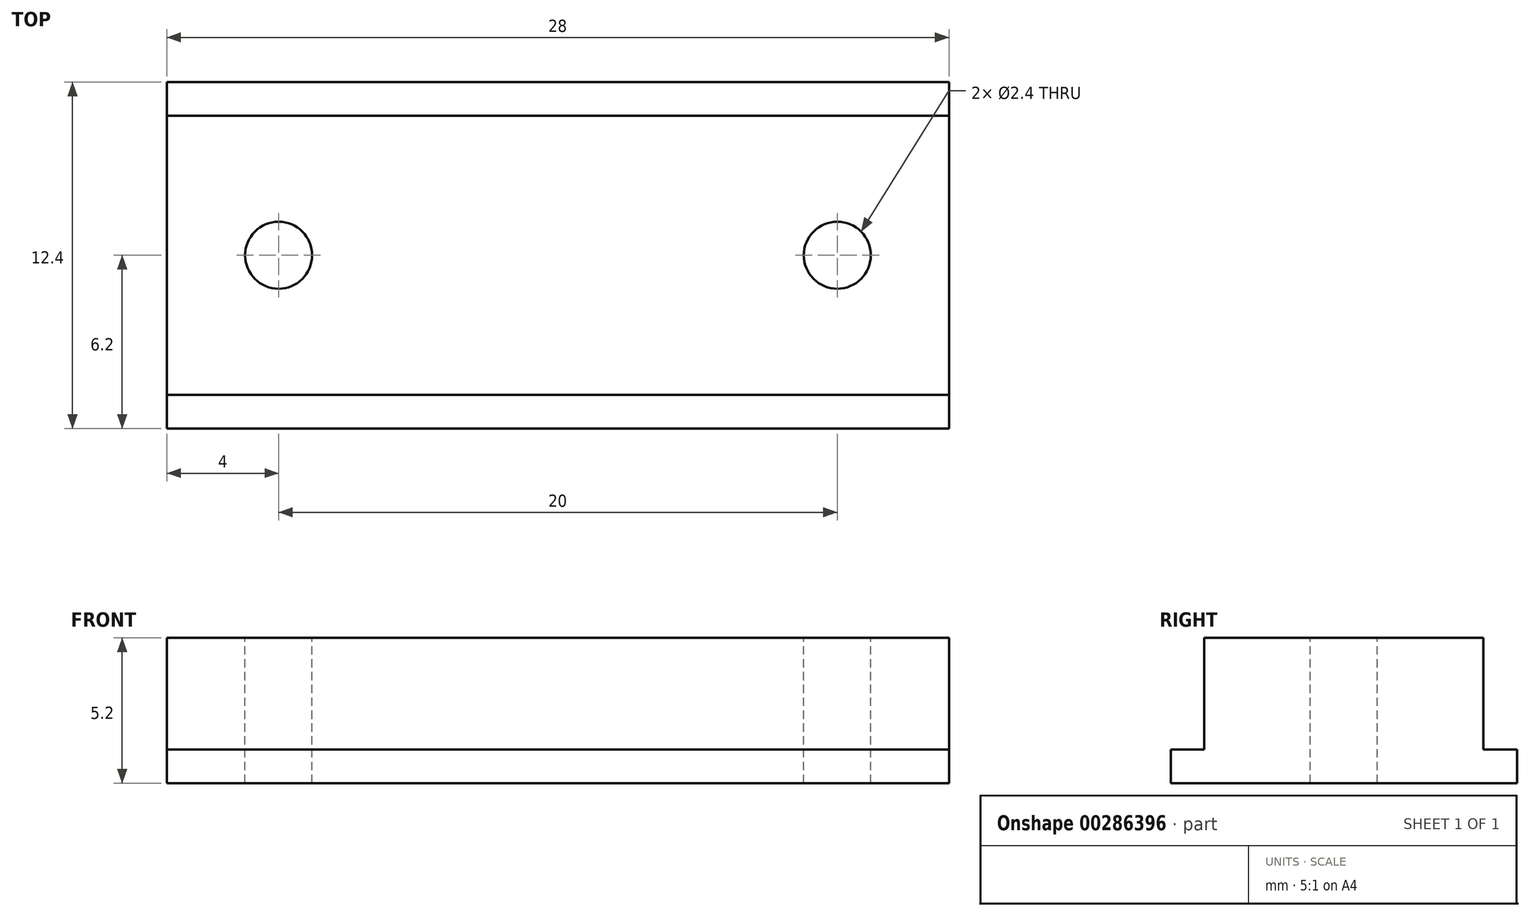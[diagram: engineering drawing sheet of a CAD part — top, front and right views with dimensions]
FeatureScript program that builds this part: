
annotation { "Feature Type Name" : "Feature", "Feature Type Description" : "" }
export const myFeature = defineFeature(function(context is Context, id is Id, definition is map)
    precondition{}
    {
        {
            var Q0;
            Q0=qCreatedBy(makeId("Front.planeOp"),FACE);
            var sketch = newSketch(context, id + "F0", { "sketchPlane" : qUnion([Q0])});
            skLineSegment(sketch, "E0.bottom", {"start": v(0, 0) * mm, "end": v(28, 0) * mm});
            skLineSegment(sketch, "E0.top", {"start": v(0, 4) * mm, "end": v(28, 4) * mm});
            skLineSegment(sketch, "E0.left", {"start": v(0, 0) * mm, "end": v(0, 4) * mm});
            skLineSegment(sketch, "E0.right", {"start": v(28, 0) * mm, "end": v(28, 4) * mm});
            skSolve(sketch);
        }
        {
            var Q0;
            Q0=makeQuery(id+"F0.imprint","IMPRINT",FACE,{"disambiguationData":[TD([[makeQuery(id+"F0.imprint","IMPRINT",EDGE,{"derivedFrom":sQuery(id+"F0.wireOp",EDGE,"E0.bottom")}),1.0]])]});
            extrude(context, id + "F1", {"entities" : qUnion([Q0]), "oppositeDirection" : true, "depth" : 10 * mm});
        }
        {
            var Q0;
            Q0=qCreatedBy(makeId("Front.planeOp"),FACE);
            var sketch = newSketch(context, id + "F2", { "sketchPlane" : qUnion([Q0])});
            skLineSegment(sketch, "E1.bottom", {"start": v(0, 0) * mm, "end": v(28, 0) * mm});
            skLineSegment(sketch, "E1.top", {"start": v(0, -1.2) * mm, "end": v(28, -1.2) * mm});
            skLineSegment(sketch, "E1.left", {"start": v(0, 0) * mm, "end": v(0, -1.2) * mm});
            skLineSegment(sketch, "E1.right", {"start": v(28, 0) * mm, "end": v(28, -1.2) * mm});
            skSolve(sketch);
        }
        {
            var Q0;
            Q0=makeQuery(id+"F2.imprint","IMPRINT",FACE,{"disambiguationData":[TD([[makeQuery(id+"F2.imprint","IMPRINT",EDGE,{"derivedFrom":sQuery(id+"F2.wireOp",EDGE,"E1.bottom")}),-1.0]])]});
            extrude(context, id + "F3", {"entities" : qUnion([Q0]), "operationType" : NewBodyOperationType.ADD, "depth" : 1.2 * mm, "hasSecondDirection" : true, "secondDirectionOppositeDirection" : true, "secondDirectionDepth" : 11.2 * mm});
        }
        {
            var Q0;
            Q0=makeQuery(id+"F1.opExtrude","SWEPT_FACE",FACE,{"disambiguationData":[OSD([sQuery(id+"F0.wireOp",EDGE,"E0.top")])]});
            var sketch = newSketch(context, id + "F4", { "sketchPlane" : qUnion([Q0])});
            skLineSegment(sketch, "E2", {"start": v(0, 5) * mm, "end": v(28, 5) * mm, "construction": true});
            skLineSegment(sketch, "E3", {"start": v(28, 5) * mm, "end": v(39.55, 5) * mm, "construction": true});
            skLineSegment(sketch, "E4", {"start": v(0, 5) * mm, "end": v(-10.34, 5) * mm, "construction": true});
            skLineSegment(sketch, "E5", {"start": v(14, 0) * mm, "end": v(14, 10) * mm, "construction": true});
            skLineSegment(sketch, "E6", {"start": v(14, 10) * mm, "end": v(14, 16.23) * mm, "construction": true});
            skLineSegment(sketch, "E7", {"start": v(14, 0) * mm, "end": v(14, -8.17) * mm, "construction": true});
            skPoint(sketch, "E8", {"position": v(24, 5) * mm});
            skPoint(sketch, "E9", {"position": v(4, 5) * mm});
            skSolve(sketch);
        }
        {
            var Q0;
            Q0=sQuery(id+"F4.wireOp",VERTEX,"E9");
            var Q1;
            Q1=sQuery(id+"F4.wireOp",VERTEX,"E8");
            var Q2;
            Q2=makeQuery(id+"F1.opExtrude","SWEPT_BODY",BODY,{"disambiguationData":[OSD([sQuery(id+"F0.wireOp",EDGE,"E0.bottom"),sQuery(id+"F0.wireOp",EDGE,"E0.top"),sQuery(id+"F0.wireOp",EDGE,"E0.left"),sQuery(id+"F0.wireOp",EDGE,"E0.right")])]});
            hole(context, id + "F5", {"style" : HoleStyle.SIMPLE, "endStyle" : HoleEndStyle.BLIND, "holeDiameter" : 2.4 * mm, "holeDepth" : 15 * mm, "tappedDepth" : 12 * mm, "tapClearance" : 3, "locations" : qUnion([Q0, Q1]), "scope" : qUnion([Q2])});
        }
    });
